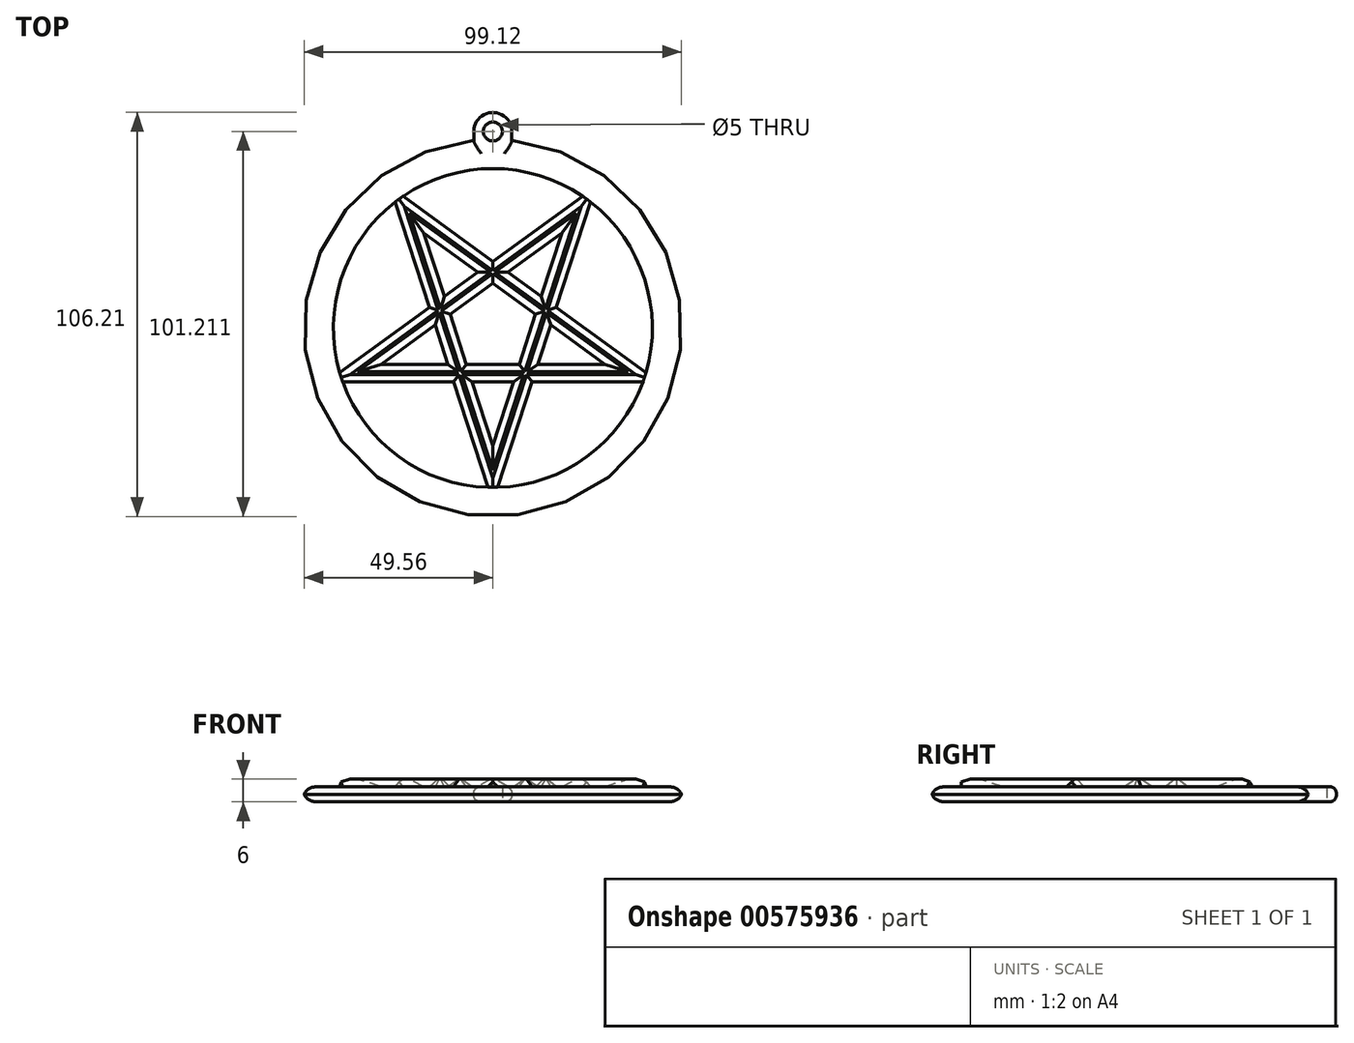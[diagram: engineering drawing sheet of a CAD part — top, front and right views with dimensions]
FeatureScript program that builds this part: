
annotation { "Feature Type Name" : "Feature", "Feature Type Description" : "" }
export const myFeature = defineFeature(function(context is Context, id is Id, definition is map)
    precondition{}
    {
        {
            var Q0;
            Q0=qCreatedBy(makeId("Top.planeOp"),FACE);
            var sketch = newSketch(context, id + "F0", { "sketchPlane" : qUnion([Q0])});
            skCircle(sketch, "E0", {"center": v(0, 0) * mm, "radius": 30.9 * mm, "construction": true});
            skLineSegment(sketch, "E1", {"start": v(0, 30.9) * mm, "end": v(0, 30.9) * mm});
            skLineSegment(sketch, "E2", {"start": v(28.48, -11.99) * mm, "end": v(28.48, -11.99) * mm});
            skLineSegment(sketch, "E3", {"start": v(-76.5, 40.8) * mm, "end": v(-76.5, 40.8) * mm});
            skLineSegment(sketch, "E4.0", {"start": v(18.16, 25) * mm, "end": v(29.39, -9.55) * mm, "construction": true});
            skLineSegment(sketch, "E4.1", {"start": v(29.39, -9.55) * mm, "end": v(0, -30.9) * mm, "construction": true});
            skLineSegment(sketch, "E4.2", {"start": v(0, -30.9) * mm, "end": v(-29.39, -9.55) * mm, "construction": true});
            skLineSegment(sketch, "E4.3", {"start": v(-29.39, -9.55) * mm, "end": v(-18.16, 25) * mm, "construction": true});
            skLineSegment(sketch, "E4.4", {"start": v(-18.16, 25) * mm, "end": v(18.16, 25) * mm, "construction": true});
            skLineSegment(sketch, "E5", {"start": v(0, -30.9) * mm, "end": v(5.43, -14.18) * mm});
            skLineSegment(sketch, "E6", {"start": v(18.16, 25) * mm, "end": v(3.94, 14.67) * mm});
            skLineSegment(sketch, "E7", {"start": v(-29.39, -9.55) * mm, "end": v(-11.81, -9.55) * mm});
            skLineSegment(sketch, "E8", {"start": v(29.39, -9.55) * mm, "end": v(15.17, 0.78) * mm});
            skLineSegment(sketch, "E9", {"start": v(-18.16, 25) * mm, "end": v(-12.73, 8.28) * mm});
            skCircle(sketch, "E10", {"center": v(0, 0) * mm, "radius": 45.9 * mm, "construction": true});
            skLineSegment(sketch, "E11.0", {"start": v(43.66, -14.18) * mm, "end": v(0, -45.9) * mm, "construction": true});
            skLineSegment(sketch, "E11.1", {"start": v(0, -45.9) * mm, "end": v(-43.66, -14.18) * mm, "construction": true});
            skLineSegment(sketch, "E11.2", {"start": v(-43.66, -14.18) * mm, "end": v(-26.98, 37.14) * mm, "construction": true});
            skLineSegment(sketch, "E11.3", {"start": v(-26.98, 37.14) * mm, "end": v(26.98, 37.14) * mm, "construction": true});
            skLineSegment(sketch, "E11.4", {"start": v(26.98, 37.14) * mm, "end": v(43.66, -14.18) * mm, "construction": true});
            skLineSegment(sketch, "E12", {"start": v(23.56, 34.65) * mm, "end": v(0, 17.53) * mm});
            skLineSegment(sketch, "E13", {"start": v(-39.43, -14.18) * mm, "end": v(-10.3, -14.18) * mm});
            skLineSegment(sketch, "E14", {"start": v(40.24, -11.7) * mm, "end": v(16.67, 5.42) * mm});
            skLineSegment(sketch, "E15", {"start": v(-25.67, 33.11) * mm, "end": v(-16.67, 5.42) * mm});
            skLineSegment(sketch, "E16", {"start": v(1.3, -41.88) * mm, "end": v(10.3, -14.18) * mm});
            skArc(sketch, "E17", {"start": v(-5, 49.65) * mm, "mid": v(0, -49.9) * mm, "end": v(5, 49.65) * mm});
            skCircle(sketch, "E18", {"center": v(0, 0) * mm, "radius": 41.9 * mm});
            skLineSegment(sketch, "E19.trimOffspring", {"start": v(12.73, 8.28) * mm, "end": v(3.94, 14.67) * mm});
            skLineSegment(sketch, "E20.trimOffspring", {"start": v(11.23, 3.65) * mm, "end": v(0, 11.8) * mm});
            skLineSegment(sketch, "E21.trimOffspring", {"start": v(12.73, 8.28) * mm, "end": v(18.16, 25) * mm});
            skLineSegment(sketch, "E22.trimOffspring", {"start": v(16.67, 5.42) * mm, "end": v(25.67, 33.11) * mm});
            skLineSegment(sketch, "E23.trimOffspring", {"start": v(0, 17.53) * mm, "end": v(-23.56, 34.65) * mm});
            skLineSegment(sketch, "E24.trimOffspring", {"start": v(-3.94, 14.67) * mm, "end": v(-12.73, 8.28) * mm});
            skLineSegment(sketch, "E25.trimOffspring", {"start": v(-3.94, 14.67) * mm, "end": v(-18.16, 25) * mm});
            skLineSegment(sketch, "E26.trimOffspring", {"start": v(0, 11.8) * mm, "end": v(-11.23, 3.65) * mm});
            skLineSegment(sketch, "E27.trimOffspring", {"start": v(-11.23, 3.65) * mm, "end": v(-6.94, -9.55) * mm});
            skLineSegment(sketch, "E28.trimOffspring", {"start": v(-16.67, 5.42) * mm, "end": v(-40.24, -11.7) * mm});
            skLineSegment(sketch, "E29.trimOffspring", {"start": v(-15.17, 0.78) * mm, "end": v(-11.81, -9.55) * mm});
            skLineSegment(sketch, "E30.trimOffspring", {"start": v(-15.17, 0.78) * mm, "end": v(-29.39, -9.55) * mm});
            skLineSegment(sketch, "E31.trimOffspring", {"start": v(-6.94, -9.55) * mm, "end": v(6.94, -9.55) * mm});
            skLineSegment(sketch, "E32.trimOffspring", {"start": v(-10.3, -14.18) * mm, "end": v(-1.3, -41.88) * mm});
            skLineSegment(sketch, "E33.trimOffspring", {"start": v(-5.43, -14.18) * mm, "end": v(0, -30.9) * mm});
            skLineSegment(sketch, "E34.trimOffspring", {"start": v(-5.43, -14.18) * mm, "end": v(5.43, -14.18) * mm});
            skLineSegment(sketch, "E35.trimOffspring", {"start": v(11.81, -9.55) * mm, "end": v(29.39, -9.55) * mm});
            skLineSegment(sketch, "E36.trimOffspring", {"start": v(11.81, -9.55) * mm, "end": v(15.17, 0.78) * mm});
            skLineSegment(sketch, "E37.trimOffspring", {"start": v(6.94, -9.55) * mm, "end": v(11.23, 3.65) * mm});
            skLineSegment(sketch, "E38.trimOffspring", {"start": v(10.3, -14.18) * mm, "end": v(39.43, -14.18) * mm});
            skLineSegment(sketch, "E39.left", {"start": v(-5, 51.65) * mm, "end": v(-5, 49.65) * mm});
            skLineSegment(sketch, "E39.right", {"start": v(5, 51.65) * mm, "end": v(5, 49.65) * mm});
            skArc(sketch, "E40", {"start": v(-5, 51.65) * mm, "mid": v(0, 56.65) * mm, "end": v(5, 51.65) * mm});
            skCircle(sketch, "E41", {"center": v(0, 51.65) * mm, "radius": 2.5 * mm});
            skSolve(sketch);
        }
        {
            var Q0;
            {var subQ8=sQuery(id+"F0.wireOp",EDGE,"E17");var subQ9=makeQuery(id+"F0.imprint","INTERSECT",VERTEX,{"derivedFrom":[subQ8,sQuery(id+"F0.wireOp",EDGE,"E39.right")]});Q0=makeQuery(id+"F0.imprint","IMPRINT",FACE,{"disambiguationData":[TD([[makeQuery(id+"F0.imprint","IMPRINT",EDGE,{"disambiguationData":[TD([[subQ9,-1.0]])],"derivedFrom":subQ8}),1.0]])]});}
            var Q1;
            Q1=makeQuery(id+"F0.imprint","IMPRINT",FACE,{"disambiguationData":[TD([[makeQuery(id+"F0.imprint","IMPRINT",EDGE,{"derivedFrom":sQuery(id+"F0.wireOp",EDGE,"E39.bottom")}),-1.0]])]});
            extrude(context, id + "F1", {"entities" : qUnion([Q0, Q1]), "depth" : 4 * mm, "offsetDistance" : 25 * mm});
        }
        {
            var Q0;
            Q0=makeQuery(id+"F1.opExtrude","CAP_EDGE",EDGE,{"disambiguationData":[OSD([sQuery(id+"F0.wireOp",EDGE,"E17")])],"isStart":false});
            var Q1;
            Q1=makeQuery(id+"F1.opExtrude","CAP_EDGE",EDGE,{"disambiguationData":[OSD([sQuery(id+"F0.wireOp",EDGE,"E17")])],"isStart":true});
            fillet(context, id + "F2", {"entities" : qUnion([Q0, Q1]), "radius" : 4 * mm, "tangentPropagation" : true, "rho" : 0.5, "crossSection" : FilletCrossSection.CONIC, "allowEdgeOverflow" : false});
        }
        {
            var Q0;
            Q0=makeQuery(id+"F1.opExtrude","CAP_EDGE",EDGE,{"disambiguationData":[OSD([sQuery(id+"F0.wireOp",EDGE,"E40")])],"isStart":false});
            var Q1;
            Q1=makeQuery(id+"F1.opExtrude","CAP_EDGE",EDGE,{"disambiguationData":[OSD([sQuery(id+"F0.wireOp",EDGE,"E39.right")])],"isStart":false});
            var Q2;
            Q2=makeQuery(id+"F1.opExtrude","CAP_EDGE",EDGE,{"disambiguationData":[OSD([sQuery(id+"F0.wireOp",EDGE,"E39.left")])],"isStart":false});
            var Q3;
            Q3=makeQuery(id+"F1.opExtrude","CAP_EDGE",EDGE,{"disambiguationData":[OSD([sQuery(id+"F0.wireOp",EDGE,"E40")])],"isStart":true});
            var Q4;
            Q4=makeQuery(id+"F1.opExtrude","CAP_EDGE",EDGE,{"disambiguationData":[OSD([sQuery(id+"F0.wireOp",EDGE,"E39.right")])],"isStart":true});
            var Q5;
            Q5=makeQuery(id+"F1.opExtrude","CAP_EDGE",EDGE,{"disambiguationData":[OSD([sQuery(id+"F0.wireOp",EDGE,"E39.left")])],"isStart":true});
            fillet(context, id + "F3", {"entities" : qUnion([Q0, Q1, Q2, Q3, Q4, Q5]), "radius" : 2 * mm, "tangentPropagation" : true, "rho" : 0.5, "crossSection" : FilletCrossSection.CONIC, "allowEdgeOverflow" : false});
        }
        {
            var Q0;
            Q0=makeQuery(id+"F0.imprint","IMPRINT",FACE,{"disambiguationData":[TD([[makeQuery(id+"F0.imprint","IMPRINT",EDGE,{"derivedFrom":sQuery(id+"F0.wireOp",EDGE,"E5")}),-1.0]])]});
            extrude(context, id + "F4", {"entities" : qUnion([Q0]), "operationType" : NewBodyOperationType.ADD, "depth" : 6 * mm, "offsetDistance" : 25 * mm});
        }
        {
            var Q0;
            Q0=makeQuery(id+"F4.opExtrude","CAP_EDGE",EDGE,{"disambiguationData":[OSD([sQuery(id+"F0.wireOp",EDGE,"E20.trimOffspring")])],"isStart":false});
            var Q1;
            Q1=makeQuery(id+"F4.opExtrude","CAP_EDGE",EDGE,{"disambiguationData":[OSD([sQuery(id+"F0.wireOp",EDGE,"E26.trimOffspring")])],"isStart":false});
            var Q2;
            Q2=makeQuery(id+"F4.opExtrude","CAP_EDGE",EDGE,{"disambiguationData":[OSD([sQuery(id+"F0.wireOp",EDGE,"E27.trimOffspring")])],"isStart":false});
            var Q3;
            Q3=makeQuery(id+"F4.opExtrude","CAP_EDGE",EDGE,{"disambiguationData":[OSD([sQuery(id+"F0.wireOp",EDGE,"E31.trimOffspring")])],"isStart":false});
            var Q4;
            Q4=makeQuery(id+"F4.opExtrude","CAP_EDGE",EDGE,{"disambiguationData":[OSD([sQuery(id+"F0.wireOp",EDGE,"E37.trimOffspring")])],"isStart":false});
            var Q5;
            Q5=makeQuery(id+"F4.opExtrude","CAP_EDGE",EDGE,{"disambiguationData":[OSD([sQuery(id+"F0.wireOp",EDGE,"E36.trimOffspring")])],"isStart":false});
            var Q6;
            Q6=makeQuery(id+"F4.opExtrude","CAP_EDGE",EDGE,{"disambiguationData":[OSD([sQuery(id+"F0.wireOp",EDGE,"E8")])],"isStart":false});
            var Q7;
            Q7=makeQuery(id+"F4.opExtrude","CAP_EDGE",EDGE,{"disambiguationData":[OSD([sQuery(id+"F0.wireOp",EDGE,"E35.trimOffspring")])],"isStart":false});
            var Q8;
            Q8=makeQuery(id+"F4.opExtrude","CAP_EDGE",EDGE,{"disambiguationData":[OSD([sQuery(id+"F0.wireOp",EDGE,"E5")])],"isStart":false});
            var Q9;
            Q9=makeQuery(id+"F4.opExtrude","CAP_EDGE",EDGE,{"disambiguationData":[OSD([sQuery(id+"F0.wireOp",EDGE,"E33.trimOffspring")])],"isStart":false});
            var Q10;
            Q10=makeQuery(id+"F4.opExtrude","CAP_EDGE",EDGE,{"disambiguationData":[OSD([sQuery(id+"F0.wireOp",EDGE,"E34.trimOffspring")])],"isStart":false});
            var Q11;
            Q11=makeQuery(id+"F4.opExtrude","CAP_EDGE",EDGE,{"disambiguationData":[OSD([sQuery(id+"F0.wireOp",EDGE,"E7")])],"isStart":false});
            var Q12;
            Q12=makeQuery(id+"F4.opExtrude","CAP_EDGE",EDGE,{"disambiguationData":[OSD([sQuery(id+"F0.wireOp",EDGE,"E30.trimOffspring")])],"isStart":false});
            var Q13;
            Q13=makeQuery(id+"F4.opExtrude","CAP_EDGE",EDGE,{"disambiguationData":[OSD([sQuery(id+"F0.wireOp",EDGE,"E29.trimOffspring")])],"isStart":false});
            var Q14;
            Q14=makeQuery(id+"F4.opExtrude","CAP_EDGE",EDGE,{"disambiguationData":[OSD([sQuery(id+"F0.wireOp",EDGE,"E24.trimOffspring")])],"isStart":false});
            var Q15;
            Q15=makeQuery(id+"F4.opExtrude","CAP_EDGE",EDGE,{"disambiguationData":[OSD([sQuery(id+"F0.wireOp",EDGE,"E25.trimOffspring")])],"isStart":false});
            var Q16;
            Q16=makeQuery(id+"F4.opExtrude","CAP_EDGE",EDGE,{"disambiguationData":[OSD([sQuery(id+"F0.wireOp",EDGE,"E9")])],"isStart":false});
            var Q17;
            Q17=makeQuery(id+"F4.opExtrude","CAP_EDGE",EDGE,{"disambiguationData":[OSD([sQuery(id+"F0.wireOp",EDGE,"E12")])],"isStart":false});
            var Q18;
            Q18=makeQuery(id+"F4.opExtrude","CAP_EDGE",EDGE,{"disambiguationData":[OSD([sQuery(id+"F0.wireOp",EDGE,"E23.trimOffspring")])],"isStart":false});
            var Q19;
            Q19=makeQuery(id+"F4.opExtrude","CAP_EDGE",EDGE,{"disambiguationData":[OSD([sQuery(id+"F0.wireOp",EDGE,"E15")])],"isStart":false});
            var Q20;
            Q20=makeQuery(id+"F4.opExtrude","CAP_EDGE",EDGE,{"disambiguationData":[OSD([sQuery(id+"F0.wireOp",EDGE,"E28.trimOffspring")])],"isStart":false});
            var Q21;
            Q21=makeQuery(id+"F4.opExtrude","CAP_EDGE",EDGE,{"disambiguationData":[OSD([sQuery(id+"F0.wireOp",EDGE,"E13")])],"isStart":false});
            var Q22;
            Q22=makeQuery(id+"F4.opExtrude","CAP_EDGE",EDGE,{"disambiguationData":[OSD([sQuery(id+"F0.wireOp",EDGE,"E32.trimOffspring")])],"isStart":false});
            var Q23;
            Q23=makeQuery(id+"F4.opExtrude","CAP_EDGE",EDGE,{"disambiguationData":[OSD([sQuery(id+"F0.wireOp",EDGE,"E16")])],"isStart":false});
            var Q24;
            Q24=makeQuery(id+"F4.opExtrude","CAP_EDGE",EDGE,{"disambiguationData":[OSD([sQuery(id+"F0.wireOp",EDGE,"E38.trimOffspring")])],"isStart":false});
            var Q25;
            Q25=makeQuery(id+"F4.opExtrude","CAP_EDGE",EDGE,{"disambiguationData":[OSD([sQuery(id+"F0.wireOp",EDGE,"E14")])],"isStart":false});
            var Q26;
            Q26=makeQuery(id+"F4.opExtrude","CAP_EDGE",EDGE,{"disambiguationData":[OSD([sQuery(id+"F0.wireOp",EDGE,"E22.trimOffspring")])],"isStart":false});
            var Q27;
            Q27=makeQuery(id+"F4.opExtrude","CAP_EDGE",EDGE,{"disambiguationData":[OSD([sQuery(id+"F0.wireOp",EDGE,"E6")])],"isStart":false});
            var Q28;
            Q28=makeQuery(id+"F4.opExtrude","CAP_EDGE",EDGE,{"disambiguationData":[OSD([sQuery(id+"F0.wireOp",EDGE,"E21.trimOffspring")])],"isStart":false});
            var Q29;
            Q29=makeQuery(id+"F4.opExtrude","CAP_EDGE",EDGE,{"disambiguationData":[OSD([sQuery(id+"F0.wireOp",EDGE,"E19.trimOffspring")])],"isStart":false});
            chamfer(context, id + "F5", {"entities" : qUnion([Q0, Q1, Q2, Q3, Q4, Q5, Q6, Q7, Q8, Q9, Q10, Q11, Q12, Q13, Q14, Q15, Q16, Q17, Q18, Q19, Q20, Q21, Q22, Q23, Q24, Q25, Q26, Q27, Q28, Q29]), "width" : 1.99 * mm});
        }
    });
